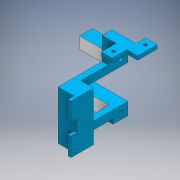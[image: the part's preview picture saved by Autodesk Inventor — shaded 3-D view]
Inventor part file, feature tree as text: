
AUTODESK INVENTOR PART (.ipt)
format: ipt  version: 2018.3 (Build 223284000, 284)  size: 457,728 bytes
history: native  units: mm
features: extrude x36, sketch x28, other x2
ambient origin geometry x8: Origin, YZ Plane, XZ Plane, XY Plane, X Axis, Y Axis, Z Axis, Center Point
bodies: Body1 (feature_tree)
feature tree (66):
  other  "Sólido1"
  extrude  "Extrusión1"  Depth=10.0mm TaperAngle=0.0deg
  extrude  "Extrusión2"  Depth=33.0mm TaperAngle=0.0deg
  extrude  "Extrusión3"  Depth=29.0mm TaperAngle=0.0deg
  extrude  "Extrusión4"  Depth=21.0mm
  extrude  "Extrusión5"  Depth=4.0mm TaperAngle=0.0deg
  extrude  "Extrusión6"  Depth=37.0mm TaperAngle=0.0deg
  extrude  "Extrusión7"  Depth=94.0mm TaperAngle=0.0deg
  extrude  "Extrusión8"  Depth=15.0mm
  extrude  "Extrusión9"  Depth=64.0mm TaperAngle=0.0deg
  extrude  "Extrusión10"  Depth=10.0mm
  extrude  "Extrusión11"  Depth=64.0mm TaperAngle=0.0deg
  extrude  "Extrusión13"  Depth=10.0mm
  extrude  "Extrusión14"  Depth=10.0mm
  extrude  "Extrusión15"  Depth=19.0mm TaperAngle=0.0deg
  extrude  "Extrusión17"  Depth=19.0mm TaperAngle=0.0deg
  extrude  "Extrusión18"  Depth=15.0mm TaperAngle=0.0deg
  extrude  "Extrusión19"  Depth=3.0mm
  extrude  "Extrusión20"  Depth=6.0mm TaperAngle=0.0deg
  extrude  "Extrusión21"  Depth=10.0mm TaperAngle=0.0deg
  extrude  "Extrusión22"  Depth=10.0mm TaperAngle=0.0deg
  extrude  "Extrusión23"  Depth=10.0mm TaperAngle=0.0deg
  extrude  "Extrusión27"  Depth=15.0mm
  extrude  "Extrusión28"  Depth=5.0mm
  extrude  "Extrusión29"  Depth=4.0mm TaperAngle=0.0deg
  extrude  "Extrusión30"  Depth=24.5mm TaperAngle=0.0deg
  extrude  "Extrusión31"  Depth=24.5mm TaperAngle=0.0deg
  extrude  "Extrusión32"  Depth=30.0mm
  extrude  "Extrusión33"  Depth=74.25mm TaperAngle=0.0deg
  sketch  "Boceto34"  dims[d106=2.0mm d107=10.0mm d108=0.0mm]
  extrude  "Extrusión35"  Depth=17.0mm TaperAngle=0.0deg
  extrude  "Extrusión36"  Depth=7.0mm
  extrude  "Extrusión38"  Depth=30.0mm TaperAngle=0.0deg
  extrude  "Extrusión39"  [1 undecoded]
  extrude  "Extrusión40"  [1 undecoded]
  extrude  "Extrusión41"  [1 undecoded]
  extrude  "Extrusión42"  [1 undecoded]
  extrude  "Extrusión43"  [1 undecoded]
  sketch  "Boceto1"  dims[d0=18.0mm d1=0.0mm d2=10.0mm d3=0.0mm]
  sketch  "Boceto2"  dims[d6=3.0mm d7=33.0mm d8=0.0mm]
  sketch  "Boceto4"  dims[d9=35.0mm d10=29.0mm d11=0.0mm]
  sketch  "Boceto5"  dims[d12=2.0mm d13=21.0mm]
  sketch  "Boceto6"  dims[d14=20.0mm d15=4.0mm d16=0.0mm]
  sketch  "Boceto7"  dims[d17=8.0mm d18=0.0mm d19=37.0mm d20=0.0mm]
  sketch  "Boceto8"  dims[d21=2.0mm d22=94.0mm d23=0.0mm]
  sketch  "Boceto9"  dims[d30=5.0mm d31=15.0mm]
  sketch  "Boceto21"  dims[d32=15.0mm d33=64.0mm d34=0.0mm]
  sketch  "Boceto22"  dims[d35=64.0mm d36=0.0mm d38=10.0mm]
  sketch  "Boceto23"  dims[d40=15.0mm d41=64.0mm d42=0.0mm]
  sketch  "Boceto24"  dims[d48=46.25mm d49=10.0mm]
  sketch  "Boceto25"  dims[d50=23.0mm d51=0.0mm d52=10.0mm]
  sketch  "Boceto27"  dims[d53=19.0mm d54=0.0mm d58=19.0mm d59=0.0mm]
  sketch  "Boceto28"  dims[d68=19.0mm d69=0.0mm d70=19.0mm d71=0.0mm]
  sketch  "Boceto29"  dims[d73=19.0mm d74=0.0mm d76=15.0mm d77=0.0mm]
  sketch  "Boceto30"  dims[d78=4.0mm d79=0.0mm d80=3.0mm]
  sketch  "Boceto31"  dims[d81=6.0mm d82=0.0mm d87=6.0mm d88=0.0mm]
  sketch  "Boceto32"  dims[d89=4.0mm d96=10.0mm d97=0.0mm]
  sketch  "Boceto33"  dims[d101=10.0mm d102=0.0mm d104=10.0mm d105=0.0mm]
  sketch  "Boceto35"  dims[d110=11.0mm d111=15.0mm]
  sketch  "Boceto37"  dims[d112=10.0mm d113=0.0mm d114=5.0mm]
  sketch  "Boceto38"  dims[d115=23.0mm d116=0.0mm d117=4.0mm d118=0.0mm]
  sketch  "Boceto39"  dims[d124=24.5mm d125=0.0mm d132=24.5mm d133=0.0mm]
  sketch  "Boceto40"  dims[d141=24.5mm d142=0.0mm d145=24.5mm d146=0.0mm]
  sketch  "Boceto41"  dims[d147=17.0mm d148=0.0mm d149=30.0mm]
  sketch  "Boceto42"  dims[d150=45.0mm d151=74.25mm d152=0.0mm d153=17.0mm d154=0.0mm d155=7.0mm d156=30.0mm d157=0.0mm]
  other  "Saliente-Extruir7"
note: 5 required parameter values undecoded (feature->parameter linkage not recoverable at this tier; creation-order binding heuristic only, values carry confidence <= 0.55)
